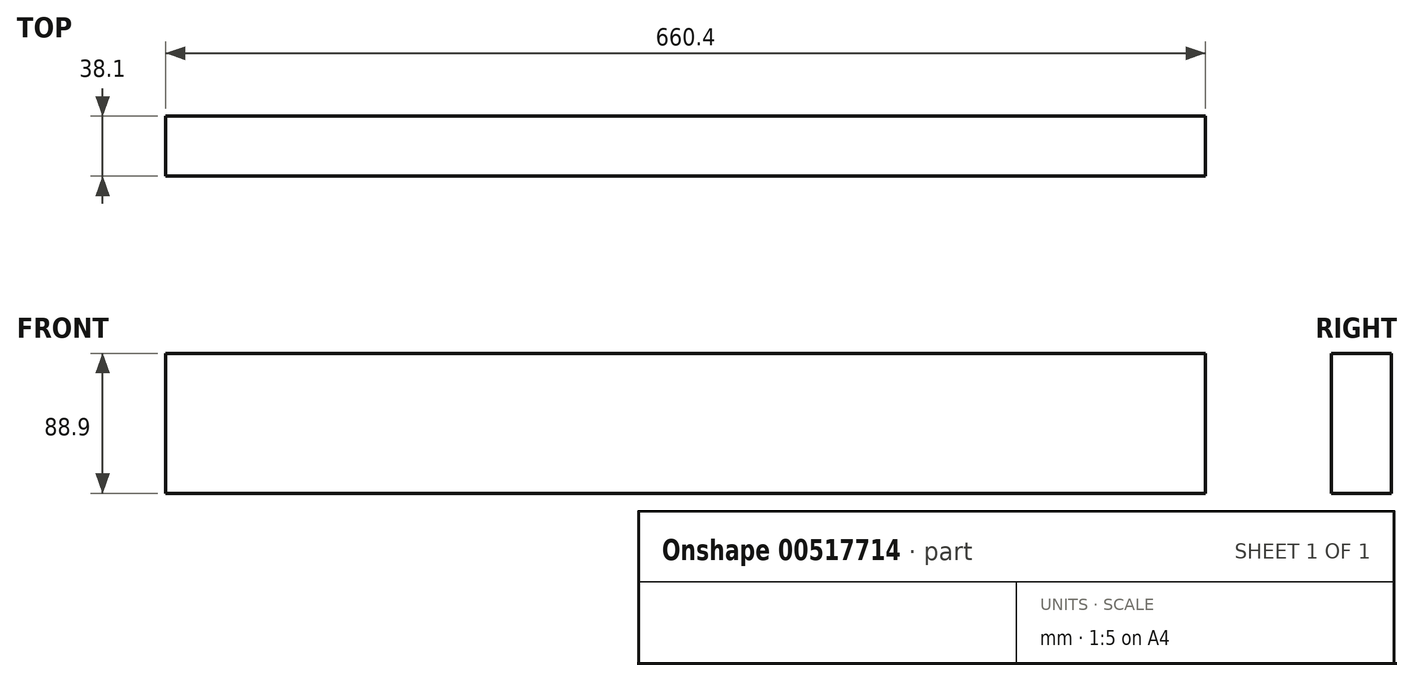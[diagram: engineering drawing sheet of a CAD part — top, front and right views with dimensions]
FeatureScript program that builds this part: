
annotation { "Feature Type Name" : "Feature", "Feature Type Description" : "" }
export const myFeature = defineFeature(function(context is Context, id is Id, definition is map)
    precondition{}
    {
        {
            var Q0;
            Q0=qCreatedBy(makeId("Front.planeOp"),FACE);
            var sketch = newSketch(context, id + "F0", { "sketchPlane" : qUnion([Q0])});
            skLineSegment(sketch, "E0.bottom", {"start": v(330.2, -44.45) * mm, "end": v(-330.2, -44.45) * mm});
            skLineSegment(sketch, "E0.top", {"start": v(330.2, 44.45) * mm, "end": v(-330.2, 44.45) * mm});
            skLineSegment(sketch, "E0.left", {"start": v(330.2, -44.45) * mm, "end": v(330.2, 44.45) * mm});
            skLineSegment(sketch, "E0.right", {"start": v(-330.2, -44.45) * mm, "end": v(-330.2, 44.45) * mm});
            skPoint(sketch, "E0.middle", {"position": v(0, 0) * mm});
            skSolve(sketch);
        }
        {
            var Q0;
            Q0 = qSketchRegion(id + "F0", true);
            extrude(context, id + "F1", {"entities" : qUnion([Q0]), "depth" : 38.1 * mm, "offsetDistance" : 25.4 * mm});
        }
    });
